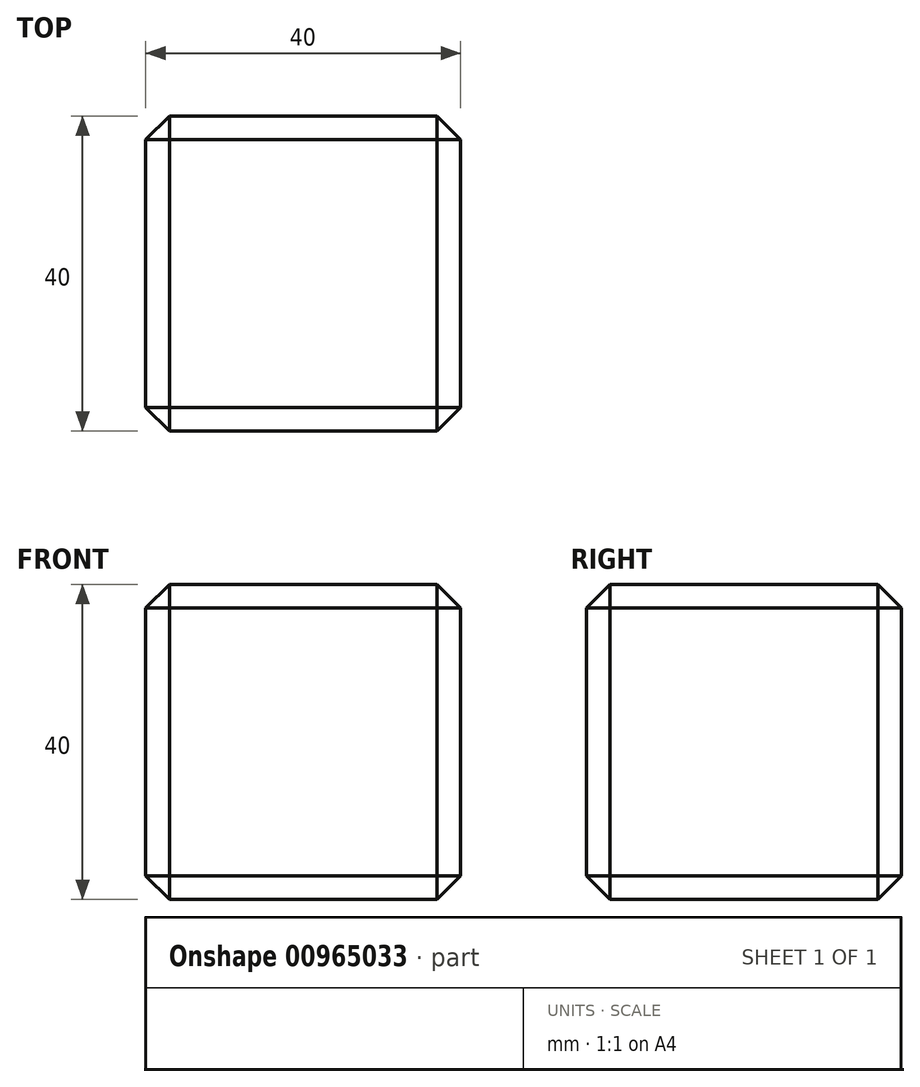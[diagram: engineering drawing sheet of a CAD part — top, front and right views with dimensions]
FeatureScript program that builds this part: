
annotation { "Feature Type Name" : "Feature", "Feature Type Description" : "" }
export const myFeature = defineFeature(function(context is Context, id is Id, definition is map)
    precondition{}
    {
        {
            var Q0;
            Q0=qCreatedBy(makeId("Top.planeOp"),FACE);
            var sketch = newSketch(context, id + "F0", { "sketchPlane" : qUnion([Q0])});
            skLineSegment(sketch, "E0.bottom", {"start": v(20, -20) * mm, "end": v(-20, -20) * mm});
            skLineSegment(sketch, "E0.top", {"start": v(20, 20) * mm, "end": v(-20, 20) * mm});
            skLineSegment(sketch, "E0.left", {"start": v(20, -20) * mm, "end": v(20, 20) * mm});
            skLineSegment(sketch, "E0.right", {"start": v(-20, -20) * mm, "end": v(-20, 20) * mm});
            skPoint(sketch, "E0.middle", {"position": v(0, 0) * mm});
            skSolve(sketch);
        }
        {
            var Q0;
            Q0 = qSketchRegion(id + "F0", true);
            extrude(context, id + "F1", {"entities" : qUnion([Q0]), "depth" : 40 * mm, "offsetDistance" : 25 * mm});
        }
        {
            var Q0;
            Q0=makeQuery(id+"F1.opExtrude","CAP_EDGE",EDGE,{"disambiguationData":[OSD([sQuery(id+"F0.wireOp",EDGE,"E0.right")])],"isStart":false});
            var Q1;
            Q1=makeQuery(id+"F1.opExtrude","CAP_EDGE",EDGE,{"disambiguationData":[OSD([sQuery(id+"F0.wireOp",EDGE,"E0.bottom")])],"isStart":false});
            var Q2;
            Q2=makeQuery(id+"F1.opExtrude","CAP_FACE",FACE,{"disambiguationData":[OSD([sQuery(id+"F0.wireOp",EDGE,"E0.bottom"),sQuery(id+"F0.wireOp",EDGE,"E0.top"),sQuery(id+"F0.wireOp",EDGE,"E0.left"),sQuery(id+"F0.wireOp",EDGE,"E0.right")])],"isStart":false});
            var Q3;
            Q3=makeQuery(id+"F1.opExtrude","SWEPT_FACE",FACE,{"disambiguationData":[OSD([sQuery(id+"F0.wireOp",EDGE,"E0.bottom")])]});
            var Q4;
            Q4=makeQuery(id+"F1.opExtrude","SWEPT_FACE",FACE,{"disambiguationData":[OSD([sQuery(id+"F0.wireOp",EDGE,"E0.right")])]});
            var Q5;
            Q5=makeQuery(id+"F1.opExtrude","SWEPT_FACE",FACE,{"disambiguationData":[OSD([sQuery(id+"F0.wireOp",EDGE,"E0.top")])]});
            var Q6;
            Q6=makeQuery(id+"F1.opExtrude","SWEPT_FACE",FACE,{"disambiguationData":[OSD([sQuery(id+"F0.wireOp",EDGE,"E0.left")])]});
            chamfer(context, id + "F2", {"entities" : qUnion([Q0, Q1, Q2, Q3, Q4, Q5, Q6]), "width" : 3 * mm, "tangentPropagation" : true});
        }
    });
